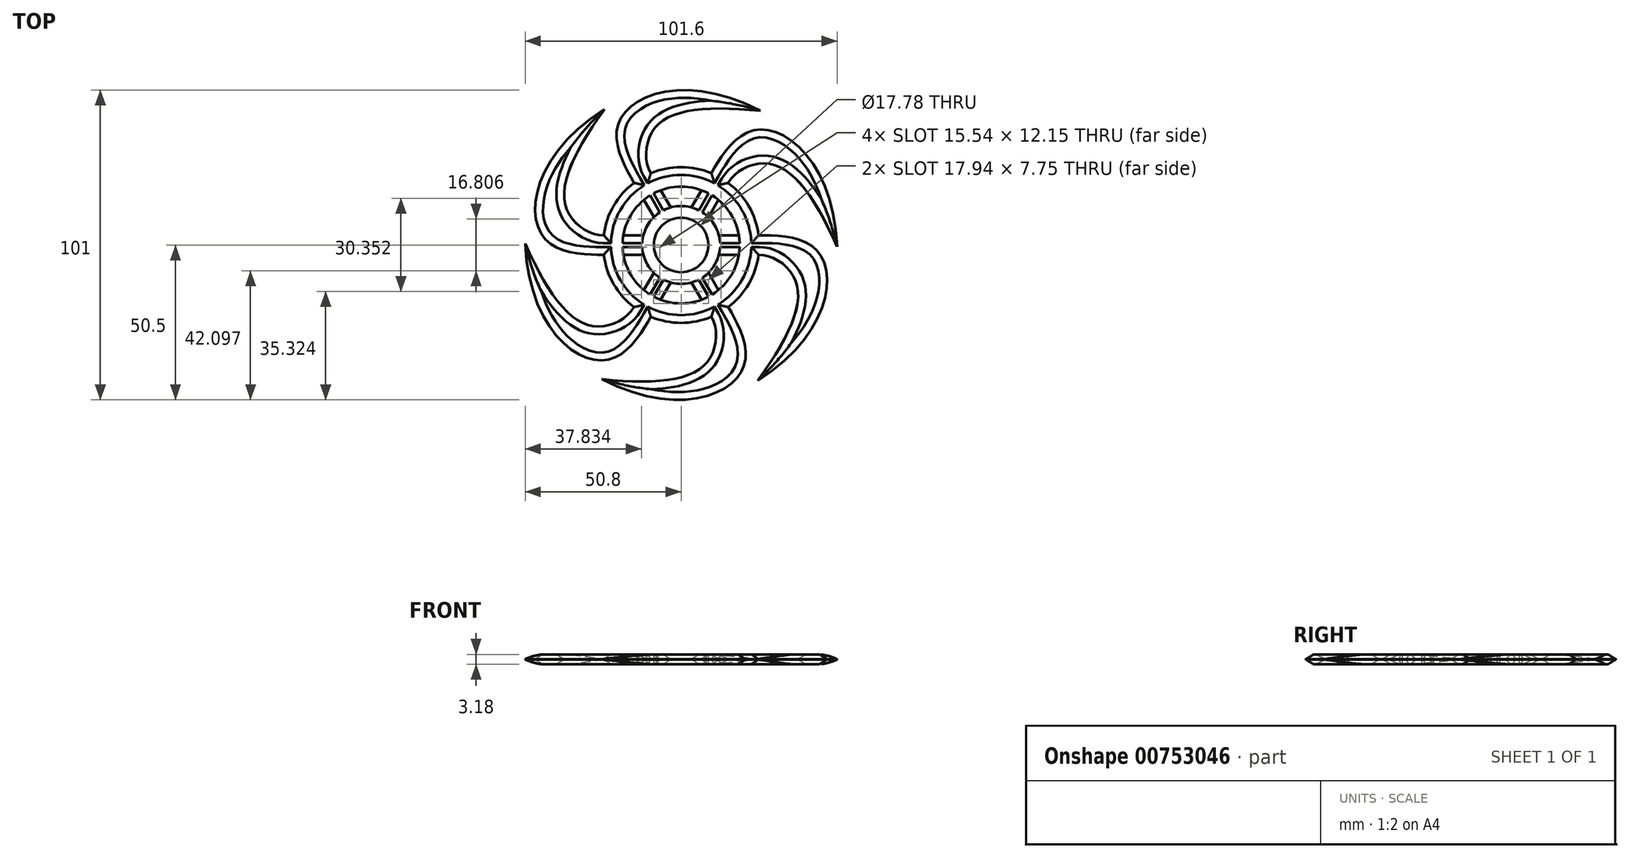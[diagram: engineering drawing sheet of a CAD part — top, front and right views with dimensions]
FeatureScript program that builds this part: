
annotation { "Feature Type Name" : "Feature", "Feature Type Description" : "" }
export const myFeature = defineFeature(function(context is Context, id is Id, definition is map)
    precondition{}
    {
        {
            var Q0;
            Q0=qCreatedBy(makeId("Top.planeOp"),FACE);
            var sketch = newSketch(context, id + "F0", { "sketchPlane" : qUnion([Q0])});
            skLineSegment(sketch, "E0.bottom", {"start": v(25.4, -3.17) * mm, "end": v(0, -3.17) * mm});
            skLineSegment(sketch, "E0.top", {"start": v(25.4, 3.18) * mm, "end": v(0, 3.18) * mm});
            skPoint(sketch, "E0.middle", {"position": v(0, 0) * mm});
            skCircle(sketch, "E1", {"center": v(0, 0) * mm, "radius": 50.8 * mm, "construction": true});
            skFitSpline(sketch, "E2", {"points": [v(25.4, 3.18) * mm, v(44.28, -1.9) * mm, v(24.96, -44.25) * mm], "startDerivative": vector(39.84, 0) * mm, "endDerivative": vector(-112.9, -71.52) * mm});
            skLineSegment(sketch, "E3.0", {"start": v(87.99, -50.8) * mm, "end": v(-87.99, -50.8) * mm});
            skPoint(sketch, "E3.0.midPoint", {"position": v(0, -50.8) * mm});
            skLineSegment(sketch, "E4.0", {"start": v(0, -50.8) * mm, "end": v(-44, 25.4) * mm, "construction": true});
            skLineSegment(sketch, "E4.1", {"start": v(-44, 25.4) * mm, "end": v(44, 25.4) * mm, "construction": true});
            skLineSegment(sketch, "E4.2", {"start": v(44, 25.4) * mm, "end": v(0, -50.8) * mm, "construction": true});
            skFitSpline(sketch, "E5", {"points": [v(25.4, -3.17) * mm, v(37.33, -11.78) * mm, v(24.96, -44.25) * mm], "startDerivative": vector(34.63, 0) * mm, "endDerivative": vector(-48.4, -66.8) * mm});
            skLineSegment(sketch, "E6", {"start": v(0, 3.17) * mm, "end": v(0, -3.17) * mm});
            skSolve(sketch);
        }
        {
            var Q0;
            Q0=makeQuery(id+"F0.imprint","IMPRINT",FACE,{"disambiguationData":[TD([[makeQuery(id+"F0.imprint","IMPRINT",EDGE,{"derivedFrom":sQuery(id+"F0.wireOp",EDGE,"E0.bottom")}),-1.0]])]});
            extrude(context, id + "F1", {"entities" : qUnion([Q0]), "depth" : 3.17 * mm, "offsetDistance" : 25.4 * mm});
        }
        {
            var Q0;
            Q0=qCreatedBy(makeId("Front.planeOp"),FACE);
            var sketch = newSketch(context, id + "F2", { "sketchPlane" : qUnion([Q0])});
            skLineSegment(sketch, "E7", {"start": v(0, 3.1) * mm, "end": v(0, 0) * mm});
            skSolve(sketch);
        }
        {
            var Q0;
            Q0=makeQuery(id+"F1.opExtrude","CAP_EDGE",EDGE,{"disambiguationData":[OSD([sQuery(id+"F0.wireOp",EDGE,"E2")])],"isStart":true});
            var Q1;
            Q1=makeQuery(id+"F1.opExtrude","CAP_EDGE",EDGE,{"disambiguationData":[OSD([sQuery(id+"F0.wireOp",EDGE,"E5")])],"isStart":true});
            var Q2;
            Q2=makeQuery(id+"F1.opExtrude","CAP_EDGE",EDGE,{"disambiguationData":[OSD([sQuery(id+"F0.wireOp",EDGE,"E2")])],"isStart":false});
            var Q3;
            Q3=makeQuery(id+"F1.opExtrude","CAP_EDGE",EDGE,{"disambiguationData":[OSD([sQuery(id+"F0.wireOp",EDGE,"E5")])],"isStart":false});
            chamfer(context, id + "F3", {"entities" : qUnion([Q0, Q1, Q2, Q3]), "chamferType" : ChamferType.TWO_OFFSETS, "width1" : 2.54 * mm, "oppositeDirection" : false, "width2" : 1.52 * mm, "tangentPropagation" : true});
        }
        {
            var Q0;
            Q0=makeQuery(id+"F1.opExtrude","SWEPT_BODY",BODY,{"disambiguationData":[OSD([sQuery(id+"F0.wireOp",EDGE,"E0.bottom"),sQuery(id+"F0.wireOp",EDGE,"E0.top"),sQuery(id+"F0.wireOp",EDGE,"E2"),sQuery(id+"F0.wireOp",EDGE,"E5"),sQuery(id+"F0.wireOp",EDGE,"E6")])]});
            var Q1;
            Q1=sQuery(id+"F2.wireOp",EDGE,"E7");
            circularPattern(context, id + "F4", {"entities" : qUnion([Q0]), "axis" : qUnion([Q1]), "angle" : 360 * degree, "instanceCount" : 6, "equalSpace" : true});
        }
        {
            var Q0;
            Q0=qCreatedBy(makeId("Top.planeOp"),FACE);
            var sketch = newSketch(context, id + "F5", { "sketchPlane" : qUnion([Q0])});
            skCircle(sketch, "E8", {"center": v(0, 0) * mm, "radius": 12.7 * mm});
            skCircle(sketch, "E9", {"center": v(0, 0) * mm, "radius": 19.05 * mm});
            skCircle(sketch, "E10", {"center": v(0, 0) * mm, "radius": 25.4 * mm});
            skSolve(sketch);
        }
        {
            var Q0;
            Q0=makeQuery(id+"F5.imprint","IMPRINT",FACE,{"disambiguationData":[TD([[makeQuery(id+"F5.imprint","IMPRINT",EDGE,{"derivedFrom":sQuery(id+"F5.wireOp",EDGE,"E8")}),1.0]])]});
            extrude(context, id + "F6", {"entities" : qUnion([Q0]), "depth" : 3.17 * mm, "offsetDistance" : 25.4 * mm});
        }
        {
            var Q0;
            Q0=makeQuery(id+"F5.imprint","IMPRINT",FACE,{"disambiguationData":[TD([[makeQuery(id+"F5.imprint","IMPRINT",EDGE,{"derivedFrom":sQuery(id+"F5.wireOp",EDGE,"E9")}),-1.0]])]});
            extrude(context, id + "F7", {"entities" : qUnion([Q0]), "depth" : 3.17 * mm, "offsetDistance" : 25.4 * mm});
        }
        {
            var Q0;
            Q0=makeQuery(id+"F7.opExtrude","CAP_EDGE",EDGE,{"disambiguationData":[OSD([sQuery(id+"F5.wireOp",EDGE,"E10")])],"isStart":true});
            var Q1;
            Q1=makeQuery(id+"F7.opExtrude","CAP_EDGE",EDGE,{"disambiguationData":[OSD([sQuery(id+"F5.wireOp",EDGE,"E10")])],"isStart":false});
            chamfer(context, id + "F8", {"entities" : qUnion([Q0, Q1]), "chamferType" : ChamferType.TWO_OFFSETS, "width1" : 1.52 * mm, "oppositeDirection" : false, "width2" : 2.54 * mm, "tangentPropagation" : true});
        }
        {
            var Q0;
            Q0=makeQuery(id+"F4.opPattern","COPY",BODY,{"derivedFrom":makeQuery(id+"F1.opExtrude","SWEPT_BODY",BODY,{"disambiguationData":[OSD([sQuery(id+"F0.wireOp",EDGE,"E0.bottom"),sQuery(id+"F0.wireOp",EDGE,"E0.top"),sQuery(id+"F0.wireOp",EDGE,"E2"),sQuery(id+"F0.wireOp",EDGE,"E5"),sQuery(id+"F0.wireOp",EDGE,"E6")])]}),"instanceName":"4"});
            var Q1;
            Q1=makeQuery(id+"F4.opPattern","COPY",BODY,{"derivedFrom":makeQuery(id+"F1.opExtrude","SWEPT_BODY",BODY,{"disambiguationData":[OSD([sQuery(id+"F0.wireOp",EDGE,"E0.bottom"),sQuery(id+"F0.wireOp",EDGE,"E0.top"),sQuery(id+"F0.wireOp",EDGE,"E2"),sQuery(id+"F0.wireOp",EDGE,"E5"),sQuery(id+"F0.wireOp",EDGE,"E6")])]}),"instanceName":"5"});
            var Q2;
            Q2=makeQuery(id+"F1.opExtrude","SWEPT_BODY",BODY,{"disambiguationData":[OSD([sQuery(id+"F0.wireOp",EDGE,"E0.bottom"),sQuery(id+"F0.wireOp",EDGE,"E0.top"),sQuery(id+"F0.wireOp",EDGE,"E2"),sQuery(id+"F0.wireOp",EDGE,"E5"),sQuery(id+"F0.wireOp",EDGE,"E6")])]});
            var Q3;
            Q3=makeQuery(id+"F4.opPattern","COPY",BODY,{"derivedFrom":makeQuery(id+"F1.opExtrude","SWEPT_BODY",BODY,{"disambiguationData":[OSD([sQuery(id+"F0.wireOp",EDGE,"E0.bottom"),sQuery(id+"F0.wireOp",EDGE,"E0.top"),sQuery(id+"F0.wireOp",EDGE,"E2"),sQuery(id+"F0.wireOp",EDGE,"E5"),sQuery(id+"F0.wireOp",EDGE,"E6")])]}),"instanceName":"1"});
            var Q4;
            Q4=makeQuery(id+"F4.opPattern","COPY",BODY,{"derivedFrom":makeQuery(id+"F1.opExtrude","SWEPT_BODY",BODY,{"disambiguationData":[OSD([sQuery(id+"F0.wireOp",EDGE,"E0.bottom"),sQuery(id+"F0.wireOp",EDGE,"E0.top"),sQuery(id+"F0.wireOp",EDGE,"E2"),sQuery(id+"F0.wireOp",EDGE,"E5"),sQuery(id+"F0.wireOp",EDGE,"E6")])]}),"instanceName":"2"});
            var Q5;
            Q5=makeQuery(id+"F4.opPattern","COPY",BODY,{"derivedFrom":makeQuery(id+"F1.opExtrude","SWEPT_BODY",BODY,{"disambiguationData":[OSD([sQuery(id+"F0.wireOp",EDGE,"E0.bottom"),sQuery(id+"F0.wireOp",EDGE,"E0.top"),sQuery(id+"F0.wireOp",EDGE,"E2"),sQuery(id+"F0.wireOp",EDGE,"E5"),sQuery(id+"F0.wireOp",EDGE,"E6")])]}),"instanceName":"3"});
            var Q6;
            Q6=makeQuery(id+"F7.opExtrude","SWEPT_BODY",BODY,{"disambiguationData":[OSD([sQuery(id+"F5.wireOp",EDGE,"E9"),sQuery(id+"F5.wireOp",EDGE,"E10")])]});
            var Q7;
            Q7=makeQuery(id+"F6.opExtrude","SWEPT_BODY",BODY,{"disambiguationData":[OSD([sQuery(id+"F5.wireOp",EDGE,"E8")])]});
            booleanBodies(context, id + "F9", {"operationType" : BooleanOperationType.UNION, "tools" : qUnion([Q0, Q1, Q2, Q3, Q4, Q5, Q6, Q7])});
        }
        {
            var Q0;
            {var subQ0=makeQuery(id+"F1.opExtrude","CAP_FACE",FACE,{"disambiguationData":[OSD([sQuery(id+"F0.wireOp",EDGE,"E0.bottom"),sQuery(id+"F0.wireOp",EDGE,"E0.top"),sQuery(id+"F0.wireOp",EDGE,"E2"),sQuery(id+"F0.wireOp",EDGE,"E5"),sQuery(id+"F0.wireOp",EDGE,"E6")])],"isStart":false});Q0=makeQuery(id+"F9.opBoolean","MERGE",FACE,{"derivedFrom":[subQ0,makeQuery(id+"F4.opPattern","COPY",FACE,{"derivedFrom":subQ0,"instanceName":"1"}),makeQuery(id+"F4.opPattern","COPY",FACE,{"derivedFrom":subQ0,"instanceName":"2"}),makeQuery(id+"F4.opPattern","COPY",FACE,{"derivedFrom":subQ0,"instanceName":"3"}),makeQuery(id+"F4.opPattern","COPY",FACE,{"derivedFrom":subQ0,"instanceName":"4"}),makeQuery(id+"F4.opPattern","COPY",FACE,{"derivedFrom":subQ0,"instanceName":"5"}),makeQuery(id+"F6.opExtrude","CAP_FACE",FACE,{"disambiguationData":[OSD([sQuery(id+"F5.wireOp",EDGE,"E8")])],"isStart":false}),makeQuery(id+"F7.opExtrude","CAP_FACE",FACE,{"disambiguationData":[OSD([sQuery(id+"F5.wireOp",EDGE,"E9"),sQuery(id+"F5.wireOp",EDGE,"E10")])],"isStart":false})]});}
            var sketch = newSketch(context, id + "F10", { "sketchPlane" : qUnion([Q0])});
            skCircle(sketch, "E11", {"center": v(0, 0) * mm, "radius": 8.9 * mm});
            skSolve(sketch);
        }
        {
            var Q0;
            Q0=makeQuery(id+"F10.imprint","IMPRINT",FACE,{"disambiguationData":[TD([[makeQuery(id+"F10.imprint","IMPRINT",EDGE,{"derivedFrom":sQuery(id+"F10.wireOp",EDGE,"E11")}),1.0]])]});
            extrude(context, id + "F11", {"entities" : qUnion([Q0]), "operationType" : NewBodyOperationType.REMOVE, "oppositeDirection" : true, "depth" : 25.4 * mm, "offsetDistance" : 25.4 * mm});
        }
    });
